# Revit family: DRF427500AP
name_source: partatom
category: Specialty Equipment
revit_build: Autodesk Revit MEP 2014 (Build: 20130308_1515(x64)
units: mm (PartAtom-declared; Revit-internal decimal feet)

## types (1)
- DRF427500AP
    Adjustable Shelves - Refrigerator = 4 ea
    Annual Energy Consumption = 629 kWy/year
    Crisper Drawers = 2 ea
    Current (A) = 6
    Defrost Process - Freezer = Frost-Free
    Deodorizing Filter = Yes
    Depth = 24 11/16"
    Description = 42-INCH Four-Door FreshZone Plus French Door
    Door = Stainless Steel
    Door Bins -Refrigerator = 6 ea
    Door Open Alarm = Yes
    ENERGY STAR® Qualified = Yes
    Freezer = -8°F (-23°C) to -5°F (-15°C)
    Freezer - Power Freeze = -8°F (-23°C)
    Freezer Drawers = 4 ea
    Freezer Gross Capacity (cu.ft.) = 6.7 cu.ft.
    Frequency (Hz) = 60
    FreshZone™ Drawer = Yes - Cheese (37°F) / Cold Drinks (33°F) / Meat (29°F)
    FreshZone™ Plus = -8°F (-23°C) to 33°F (1°C)
    FreshZone™ Plus Compartment = Yes - Converts from freezer -8°F to to refrigerator 33°F
    Full Extension Drawers at 90º Door Opening Angle = Yes
    Full Width Shelves - Refrigerator = 1 ea
    Handle = Stainless Steel
    Height = 83 3/8"
    Icemaker = Dual Icemaker for Standard and Cocktail Ice™
    Interior Material = SteelCool™ Interior
    Internal Water Dispenser = Yes
    Lighting = 3DLighting™
    Manufacturer = Dacor
    Model = DRF427500AP
    Panel Ready = Yes
    Plug Type = 120 V, 3 Prong
    Power Cool - Refrigerator = Yes
    Power Cord Length (in.) = 78 3/4"
    Power Freeze - Freezer = Yes
    Push-To-Open™ Door Assist = No
    Refrigerator = 34°F (1°C) to 44°F (7°C)
    Refrigerator - Power Cool = 34°F (1°C)
    Refrigerator Gross Capacity (cu.ft.) = 16.8 cu. ft.
    Shelf Material - Refrigerator = Tempered Glass Shelves w/Metal Trim
    Special Modes = Sabbath Mode
    Support = Plastic-Black
    Total Unit Gross Capacity (cu.ft.) - AHAM = 23.5 cu. ft.
    Triple Cooling (3 evaporators,2 compressors) = Yes
    Unit = Stainless Steel
    Volts (V) = 115
    Width = 41 3/4"
    iQ Remote Diagnostics™ (Wi-Fi) = Yes
    iQ RemoteView™ Camera = Yes

## geometry (parser evidence)
native form markers: Sweep x1
no freeform markers — native parametric forms only
